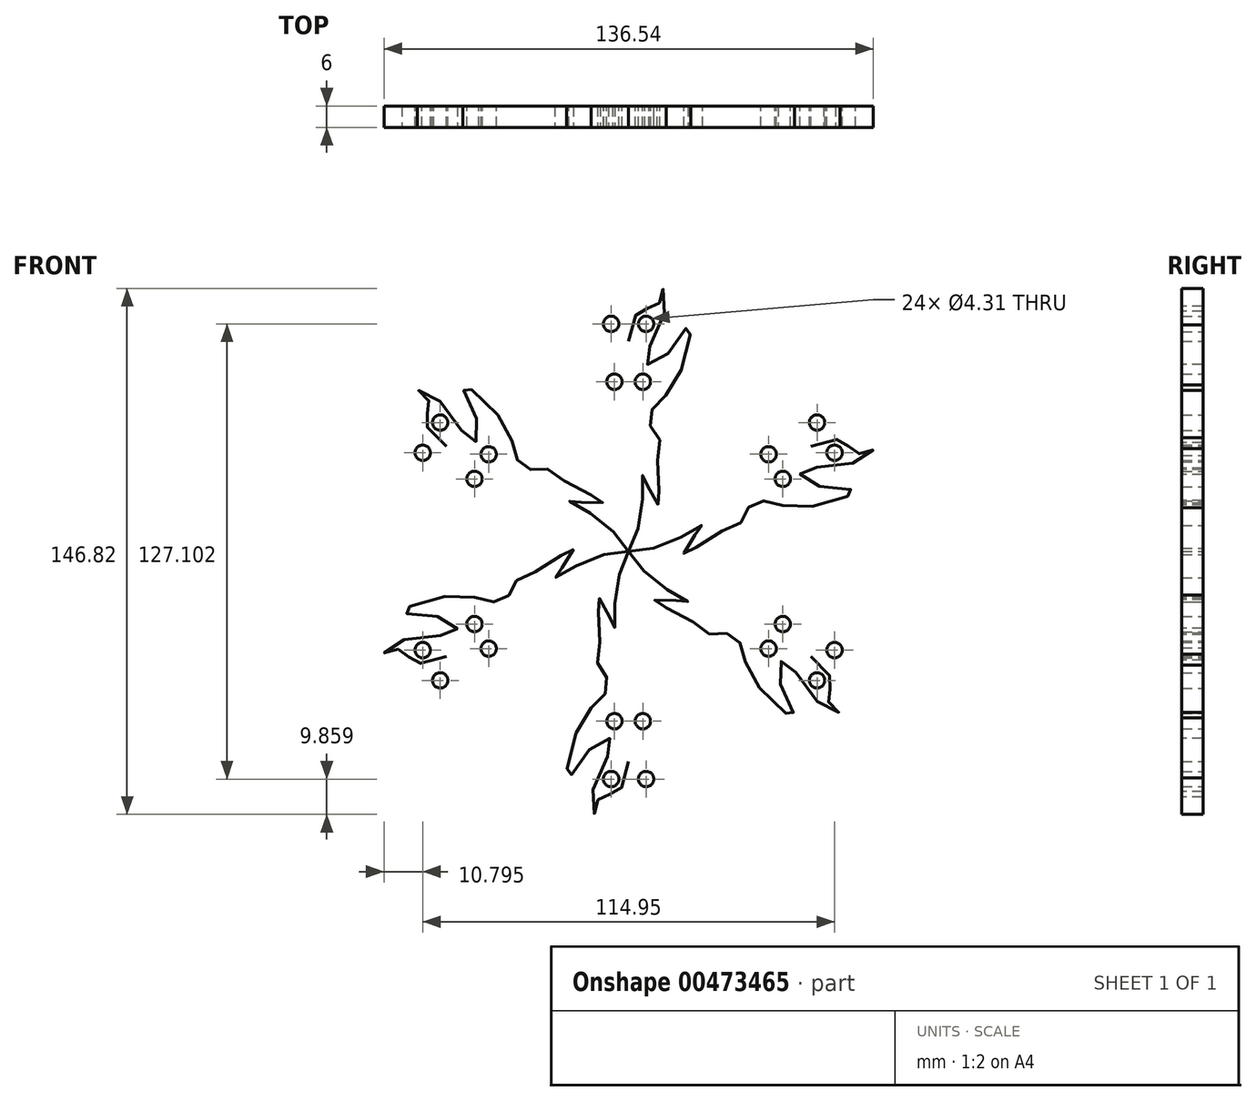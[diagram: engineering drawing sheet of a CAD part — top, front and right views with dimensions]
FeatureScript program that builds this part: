
annotation { "Feature Type Name" : "Feature", "Feature Type Description" : "" }
export const myFeature = defineFeature(function(context is Context, id is Id, definition is map)
    precondition{}
    {
        {
            var Q0;
            Q0=qCreatedBy(makeId("Front.planeOp"),FACE);
            var sketch = newSketch(context, id + "F0", { "sketchPlane" : qUnion([Q0])});
            skLineSegment(sketch, "E0", {"start": v(0, 0) * mm, "end": v(0, 68.43) * mm, "construction": true});
            skFitSpline(sketch, "E1", {"points": [v(0, 58.67) * mm, v(3.05, 68.43) * mm, v(7.62, 67.2) * mm, v(9.14, 73.3) * mm, v(10.36, 68.43) * mm, v(4.57, 52.88) * mm, v(9.75, 54.1) * mm, v(17.07, 63.25) * mm, v(13.41, 47.7) * mm, v(7.32, 40.7) * mm, v(5.8, 35.81) * mm, v(8.53, 31.55) * mm, v(7.92, 23.62) * mm, v(8.53, 12.95) * mm, v(5.49, 17.83) * mm, v(3.96, 21.49) * mm, v(3.66, 11.43) * mm, v(0, 0) * mm], "startDerivative": vector(95.22, 92.78) * mm, "endDerivative": vector(-64.83, -137.6) * mm});
            skCircle(sketch, "E2", {"center": v(3.96, 47.4) * mm, "radius": 2.16 * mm});
            skCircle(sketch, "E3", {"center": v(4.88, 63.55) * mm, "radius": 2.16 * mm});
            skFitSpline(sketch, "E4.MirrorCS", {"points": [v(0, 58.67) * mm, v(-3.05, 68.43) * mm, v(-7.62, 67.2) * mm, v(-9.14, 73.3) * mm, v(-10.36, 68.43) * mm, v(-4.57, 52.88) * mm, v(-9.75, 54.1) * mm, v(-17.07, 63.25) * mm, v(-13.41, 47.7) * mm, v(-7.32, 40.7) * mm, v(-5.8, 35.81) * mm, v(-8.53, 31.55) * mm, v(-7.92, 23.62) * mm, v(-8.53, 12.95) * mm, v(-5.49, 17.83) * mm, v(-3.96, 21.49) * mm, v(-3.66, 11.43) * mm, v(0, 0) * mm], "startDerivative": vector(-95.22, 92.78) * mm, "endDerivative": vector(64.83, -137.6) * mm});
            skCircle(sketch, "E5.MirrorC", {"center": v(-3.96, 47.4) * mm, "radius": 2.16 * mm});
            skCircle(sketch, "E6.MirrorC", {"center": v(-4.88, 63.55) * mm, "radius": 2.16 * mm});
            skSolve(sketch);
        }
        {
            var Q0;
            Q0 = qSketchRegion(id + "F0", true);
            extrude(context, id + "F1", {"entities" : qUnion([Q0]), "depth" : 6 * mm});
        }
        {
            var Q0;
            Q0=qCreatedBy(makeId("Right.planeOp"),FACE);
            var sketch = newSketch(context, id + "F2", { "sketchPlane" : qUnion([Q0])});
            skLineSegment(sketch, "E7", {"start": v(0, 0) * mm, "end": v(-64.62, 0) * mm, "construction": true});
            skSolve(sketch);
        }
        {
            var Q0;
            Q0=makeQuery(id+"F1.opExtrude","SWEPT_BODY",BODY,{"disambiguationData":[OSD([sQuery(id+"F0.wireOp",EDGE,"E1"),sQuery(id+"F0.wireOp",EDGE,"E2"),sQuery(id+"F0.wireOp",EDGE,"E3"),sQuery(id+"F0.wireOp",EDGE,"E4.MirrorCS"),sQuery(id+"F0.wireOp",EDGE,"E5.MirrorC"),sQuery(id+"F0.wireOp",EDGE,"E6.MirrorC")])]});
            var Q1;
            Q1=sQuery(id+"F2.wireOp",EDGE,"E7");
            circularPattern(context, id + "F3", {"entities" : qUnion([Q0]), "axis" : qUnion([Q1]), "angle" : 360 * degree, "instanceCount" : 6, "equalSpace" : true});
        }
    });
